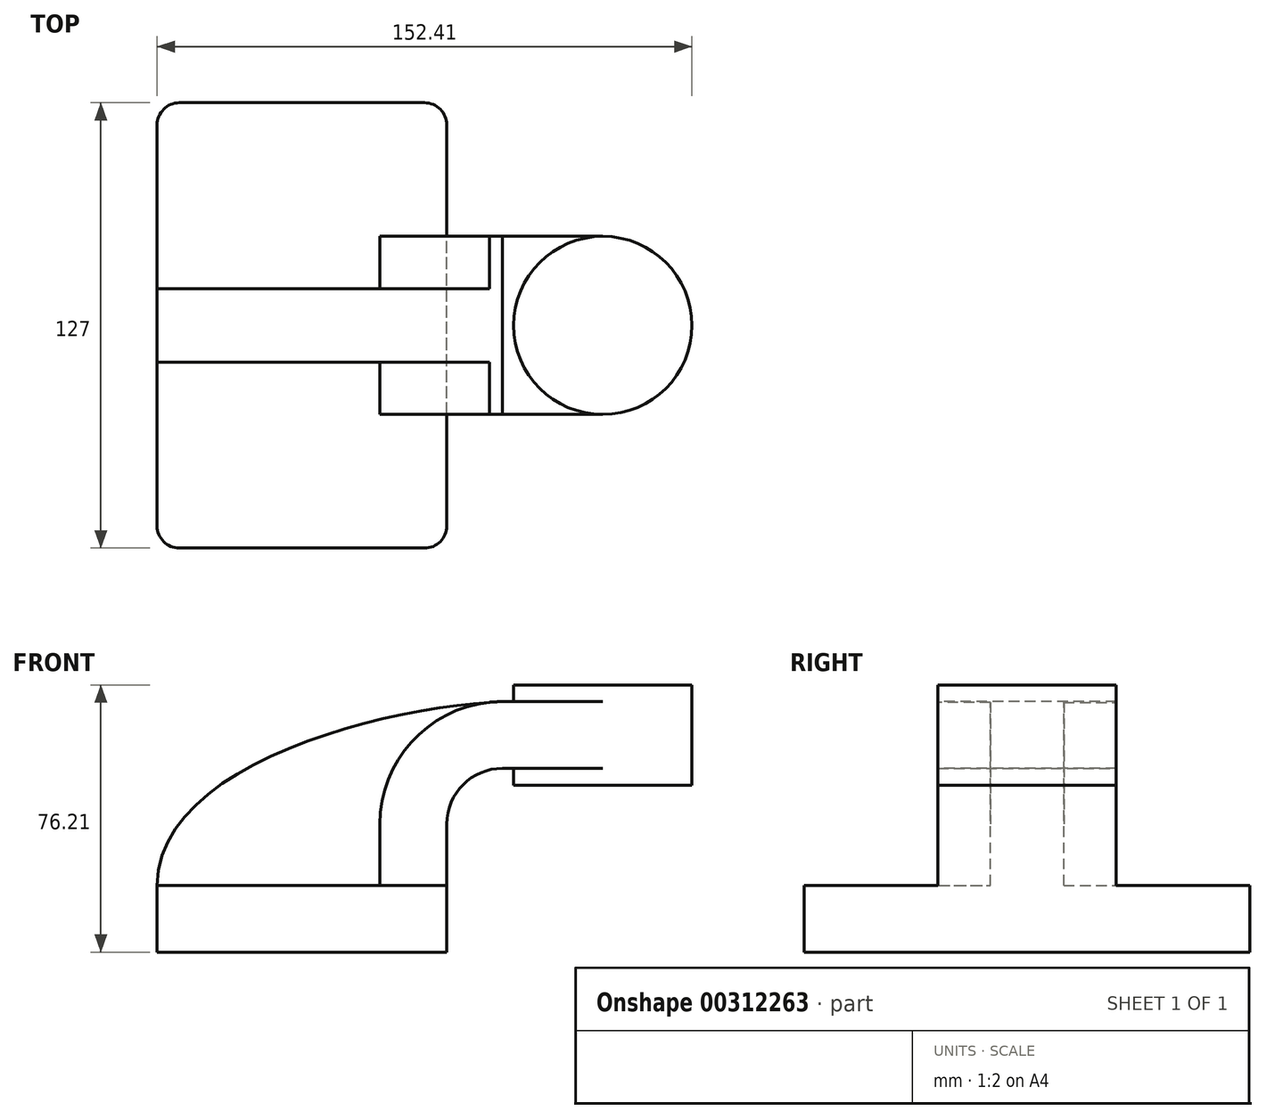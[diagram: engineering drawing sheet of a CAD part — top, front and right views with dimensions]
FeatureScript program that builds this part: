
annotation { "Feature Type Name" : "Feature", "Feature Type Description" : "" }
export const myFeature = defineFeature(function(context is Context, id is Id, definition is map)
    precondition{}
    {
        {
            var Q0;
            Q0=qCreatedBy(makeId("Front.planeOp"),FACE);
            var sketch = newSketch(context, id + "F0", { "sketchPlane" : qUnion([Q0])});
            skLineSegment(sketch, "E0.bottom", {"start": v(41.28, 9.52) * mm, "end": v(-41.28, 9.53) * mm});
            skLineSegment(sketch, "E0.top", {"start": v(41.28, -9.53) * mm, "end": v(-41.27, -9.52) * mm});
            skLineSegment(sketch, "E0.left", {"start": v(41.28, 9.52) * mm, "end": v(41.28, -9.53) * mm});
            skLineSegment(sketch, "E0.right", {"start": v(-41.28, 9.53) * mm, "end": v(-41.28, -9.52) * mm});
            skPoint(sketch, "E0.middle", {"position": v(0, 0) * mm});
            skLineSegment(sketch, "E1.bottom", {"start": v(111.12, 38.1) * mm, "end": v(60.32, 38.1) * mm});
            skLineSegment(sketch, "E1.top", {"start": v(111.12, 66.68) * mm, "end": v(60.32, 66.68) * mm});
            skLineSegment(sketch, "E1.left", {"start": v(111.12, 38.1) * mm, "end": v(111.12, 66.68) * mm});
            skLineSegment(sketch, "E1.right", {"start": v(60.32, 38.1) * mm, "end": v(60.32, 66.68) * mm});
            skPoint(sketch, "E1.middle", {"position": v(85.72, 52.39) * mm});
            skLineSegment(sketch, "E2", {"start": v(41.27, 9.52) * mm, "end": v(41.27, 27) * mm});
            skLineSegment(sketch, "E3", {"start": v(41.28, 27) * mm, "end": v(41.28, 27) * mm});
            skArc(sketch, "E4", {"start": v(41.28, 27) * mm, "mid": v(45.92, 38.23) * mm, "end": v(57.15, 42.88) * mm});
            skLineSegment(sketch, "E5", {"start": v(57.15, 42.88) * mm, "end": v(85.72, 42.88) * mm});
            skLineSegment(sketch, "E6.0", {"start": v(57.15, 61.93) * mm, "end": v(85.72, 61.93) * mm});
            skArc(sketch, "E6.1", {"start": v(22.23, 27) * mm, "mid": v(32.45, 51.7) * mm, "end": v(57.15, 61.93) * mm});
            skLineSegment(sketch, "E6.2", {"start": v(22.22, 9.52) * mm, "end": v(22.22, 27) * mm});
            skLineSegment(sketch, "E7", {"start": v(85.72, 66.68) * mm, "end": v(85.72, 38.1) * mm});
            skFitSpline(sketch, "E8", {"points": [v(-41.28, 9.53) * mm, v(57.15, 61.93) * mm], "startDerivative": vector(0.17, 105) * mm, "endDerivative": vector(96.36, 3.69) * mm});
            skSolve(sketch);
        }
        {
            var Q0;
            Q0=makeQuery(id+"F0.imprint","IMPRINT",FACE,{"disambiguationData":[TD([[makeQuery(id+"F0.imprint","IMPRINT",EDGE,{"derivedFrom":sQuery(id+"F0.wireOp",EDGE,"E0.top")}),-1.0]])]});
            extrude(context, id + "F1", {"entities" : qUnion([Q0]), "endBound" : BoundingType.SYMMETRIC, "depth" : 127 * mm});
        }
        {
            var Q0;
            {var subQ1=sQuery(id+"F0.wireOp",EDGE,"E2");Q0=makeQuery(id+"F0.imprint","IMPRINT",FACE,{"disambiguationData":[TD([[makeQuery(id+"F0.imprint","IMPRINT",EDGE,{"derivedFrom":subQ1}),1.0]])]});}
            var Q1;
            {var subQ0=sQuery(id+"F0.wireOp",EDGE,"E5");var subQ1=sQuery(id+"F0.wireOp",EDGE,"E1.right");var subQ2=makeQuery(id+"F0.imprint","INTERSECT",VERTEX,{"derivedFrom":[subQ1,subQ0]});Q1=makeQuery(id+"F0.imprint","IMPRINT",FACE,{"disambiguationData":[TD([[makeQuery(id+"F0.imprint","IMPRINT",EDGE,{"disambiguationData":[TD([[subQ2,-1.0]])],"derivedFrom":subQ1}),-1.0]])]});}
            extrude(context, id + "F2", {"entities" : qUnion([Q0, Q1]), "operationType" : NewBodyOperationType.ADD, "endBound" : BoundingType.SYMMETRIC, "depth" : 50.8 * mm});
        }
        {
            var Q0;
            {var subQ3=sQuery(id+"F0.wireOp",EDGE,"E6.2");Q0=makeQuery(id+"F0.imprint","IMPRINT",FACE,{"disambiguationData":[TD([[makeQuery(id+"F0.imprint","IMPRINT",EDGE,{"derivedFrom":subQ3}),1.0]])]});}
            extrude(context, id + "F3", {"entities" : qUnion([Q0]), "operationType" : NewBodyOperationType.ADD, "endBound" : BoundingType.SYMMETRIC, "depth" : 20.95 * mm});
        }
        {
            var Q0;
            {var subQ0=sQuery(id+"F0.wireOp",EDGE,"E1.left");Q0=makeQuery(id+"F0.imprint","IMPRINT",FACE,{"disambiguationData":[TD([[makeQuery(id+"F0.imprint","IMPRINT",EDGE,{"derivedFrom":subQ0}),1.0]])]});}
            var Q1;
            Q1=sQuery(id+"F0.wireOp",EDGE,"E7");
            revolve(context, id + "F4", {"operationType" : NewBodyOperationType.ADD, "entities" : qUnion([Q0]), "axis" : qUnion([Q1]), "revolveType" : RevolveType.FULL});
        }
        {
            var Q0;
            Q0=makeQuery(id+"F1.opExtrude","CAP_EDGE",EDGE,{"disambiguationData":[OSD([sQuery(id+"F0.wireOp",EDGE,"E0.right")])],"isStart":true});
            var Q1;
            Q1=makeQuery(id+"F1.opExtrude","CAP_EDGE",EDGE,{"disambiguationData":[OSD([sQuery(id+"F0.wireOp",EDGE,"E0.right")])],"isStart":false});
            var Q2;
            Q2=makeQuery(id+"F1.opExtrude","CAP_EDGE",EDGE,{"disambiguationData":[OSD([sQuery(id+"F0.wireOp",EDGE,"E0.left")])],"isStart":false});
            var Q3;
            Q3=makeQuery(id+"F1.opExtrude","CAP_EDGE",EDGE,{"disambiguationData":[OSD([sQuery(id+"F0.wireOp",EDGE,"E0.left")])],"isStart":true});
            fillet(context, id + "F5", {"entities" : qUnion([Q0, Q1, Q2, Q3]), "radius" : 6.35 * mm, "tangentPropagation" : true, "allowEdgeOverflow" : false});
        }
    });
